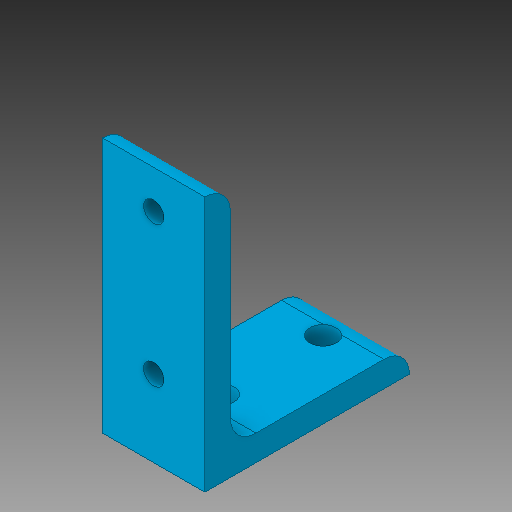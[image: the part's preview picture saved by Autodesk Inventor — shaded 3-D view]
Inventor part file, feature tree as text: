
AUTODESK INVENTOR PART (.ipt)
format: ipt  version: 2017 SP1 (Build 210196100, 196)  size: 133,120 bytes
history: native  units: in
note: dims shown in document units (in); Inventor stores cm internally (conversion verified against a paired STEP export)
features: extrude x3, sketch x3, projected_geometry x1
ambient origin geometry x8: Origin, YZ Plane, XZ Plane, XY Plane, X Axis, Y Axis, Z Axis, Center Point
bodies: Solid1 (feature_tree)
feature tree (7):
  extrude  "Extrusion1"  Depth=0.25in
  extrude  "Extrusion2"  Depth=0.2in
  extrude  "Extrusion3"  Depth=0.655in
  sketch  "Sketch1"  dims[d0=0.25in d1=2.5in]
  sketch  "Sketch2"  dims[d2=1.0in d3=0.0in d4=0.2in]
  projected_geometry  "Projected Loop1"
  sketch  "Sketch3"  dims[d5=0.5in d6=0.375in d7=1.0in d8=0.0in d9=0.26in d12=1.0in d13=0.0in d14=0.655in d15=1.0in d16=2.0in]
